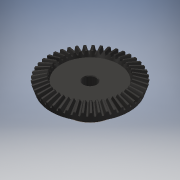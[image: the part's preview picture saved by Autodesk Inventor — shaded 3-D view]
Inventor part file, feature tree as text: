
AUTODESK INVENTOR PART (.ipt)
format: ipt  version: 2019.3 (Build 233278000, 278)  size: 2,374,144 bytes
history: native  units: in
note: dims shown in document units (in); Inventor stores cm internally (conversion verified against a paired STEP export)
features: extrude x2, sketch x2, imported_body x1
ambient origin geometry x8: Origin, YZ Plane, XZ Plane, XY Plane, X Axis, Y Axis, Z Axis, Center Point
bodies: Solid1 (feature_tree)
feature tree (5):
  extrude  "Extrusion1"  Depth=0.5in
  extrude  "Extrusion2"  [1 undecoded]
  sketch  "Sketch1"  dims[d0=0.3937in d1=0.0in d2=0.5in]
  sketch  "Sketch2"  dims[d3=0.3937in d4=0.0in]
  imported_body  "Base1"
note: 1 required parameter value undecoded (feature->parameter linkage not recoverable at this tier; creation-order binding heuristic only, values carry confidence <= 0.55)
